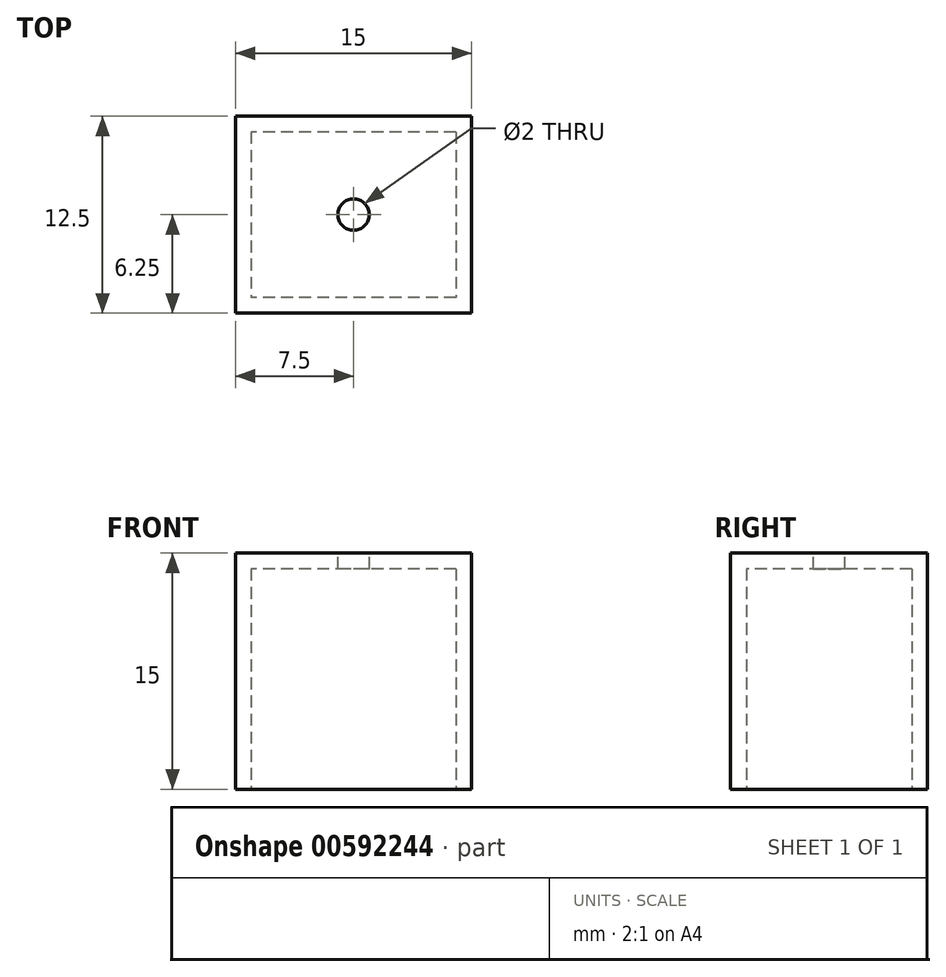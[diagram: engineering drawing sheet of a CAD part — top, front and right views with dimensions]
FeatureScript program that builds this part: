
annotation { "Feature Type Name" : "Feature", "Feature Type Description" : "" }
export const myFeature = defineFeature(function(context is Context, id is Id, definition is map)
    precondition{}
    {
        {
            var Q0;
            Q0=qCreatedBy(makeId("Top.planeOp"),FACE);
            var sketch = newSketch(context, id + "F0", { "sketchPlane" : qUnion([Q0])});
            skLineSegment(sketch, "E0.bottom", {"start": v(7.5, 6.25) * mm, "end": v(-7.5, 6.25) * mm});
            skLineSegment(sketch, "E0.top", {"start": v(7.5, -6.25) * mm, "end": v(-7.5, -6.25) * mm});
            skLineSegment(sketch, "E0.left", {"start": v(7.5, 6.25) * mm, "end": v(7.5, -6.25) * mm});
            skLineSegment(sketch, "E0.right", {"start": v(-7.5, 6.25) * mm, "end": v(-7.5, -6.25) * mm});
            skPoint(sketch, "E0.middle", {"position": v(0, 0) * mm});
            skSolve(sketch);
        }
        {
            var Q0;
            Q0=makeQuery(id+"F0.imprint","IMPRINT",FACE,{"disambiguationData":[TD([[makeQuery(id+"F0.imprint","IMPRINT",EDGE,{"derivedFrom":sQuery(id+"F0.wireOp",EDGE,"E0.bottom")}),1.0]])]});
            extrude(context, id + "F1", {"entities" : qUnion([Q0]), "depth" : 15 * mm, "offsetDistance" : 25 * mm});
        }
        {
            var Q0;
            Q0=makeQuery(id+"F1.opExtrude","CAP_FACE",FACE,{"disambiguationData":[OSD([sQuery(id+"F0.wireOp",EDGE,"E0.bottom"),sQuery(id+"F0.wireOp",EDGE,"E0.top"),sQuery(id+"F0.wireOp",EDGE,"E0.left"),sQuery(id+"F0.wireOp",EDGE,"E0.right")])],"isStart":true});
            shell(context, id + "F2", {"entities" : qUnion([Q0]), "thickness" : 1 * mm});
        }
        {
            var Q0;
            Q0=makeQuery(id+"F1.opExtrude","CAP_FACE",FACE,{"disambiguationData":[OSD([sQuery(id+"F0.wireOp",EDGE,"E0.bottom"),sQuery(id+"F0.wireOp",EDGE,"E0.top"),sQuery(id+"F0.wireOp",EDGE,"E0.left"),sQuery(id+"F0.wireOp",EDGE,"E0.right")])],"isStart":false});
            var sketch = newSketch(context, id + "F3", { "sketchPlane" : qUnion([Q0])});
            skPoint(sketch, "E1", {"position": v(0, 0) * mm});
            skSolve(sketch);
        }
        {
            var Q0;
            Q0=sQuery(id+"F3.wireOp",VERTEX,"E1");
            var Q1;
            Q1=makeQuery(id+"F1.opExtrude","SWEPT_BODY",BODY,{"disambiguationData":[OSD([sQuery(id+"F0.wireOp",EDGE,"E0.bottom"),sQuery(id+"F0.wireOp",EDGE,"E0.top"),sQuery(id+"F0.wireOp",EDGE,"E0.left"),sQuery(id+"F0.wireOp",EDGE,"E0.right")])]});
            hole(context, id + "F4", {"style" : HoleStyle.SIMPLE, "endStyle" : HoleEndStyle.THROUGH, "holeDiameter" : 2 * mm, "majorDiameter" : 5 * mm, "isTappedThrough" : true, "tappedDepth" : 12 * mm, "tapClearance" : 3, "startFromSketch" : true, "locations" : qUnion([Q0]), "scope" : qUnion([Q1])});
        }
    });
